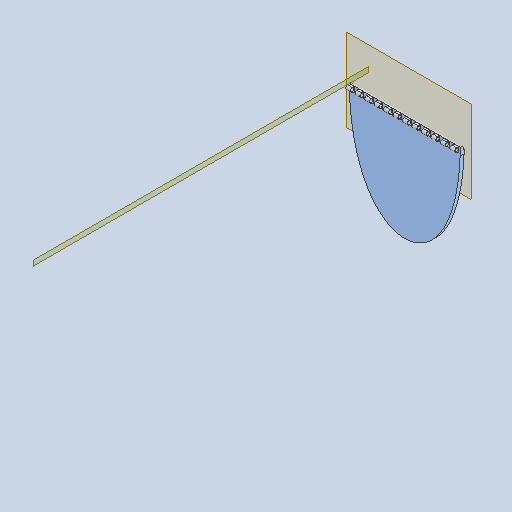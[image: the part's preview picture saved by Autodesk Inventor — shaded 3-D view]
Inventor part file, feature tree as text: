
AUTODESK INVENTOR PART (.ipt)
format: ipt  version: 2023 (Build 270158030, 158C)  size: 225,792 bytes
history: native  units: mm
features: other x4, plane x2, extrude x2, sketch x2, fillet x1, pattern_linear x1, reference x1
ambient origin geometry x8: Origin, YZ Plane, XZ Plane, XY Plane, X Axis, Y Axis, Z Axis, Center Point
bodies: Body1 (feature_tree)
feature tree (13):
  other  "back-flap"
  plane  "Work Plane1"
  extrude  "Extrusion1"  Depth=850.0mm
  plane  "Work Plane2"
  extrude  "Extrusion2"  Depth=30.0mm
  fillet  "Fillet1"  Radius=30.0mm
  pattern_linear  "Rectangular Pattern1"  Count1=35  [1 undecoded]
  sketch  "Sketch1"  dims[d0=50.0mm d1=850.0mm]
  reference  "Reference1"
  sketch  "Sketch3"  dims[d2=700.0mm d3=30.0mm d4=30.0mm d5=350.0mm d6=350.0mm d7=25.0mm d8=0.0mm d11=12.5mm d12=2.5mm d13=20.0mm d14=10.0mm d15=3.0mm d16=25.0mm d17=14.0mm d18=12.5mm d19=30.0mm d20=0.0mm d21=25.0mm d22=120.0mm d24=60.0mm]
  other  "<userpath>\Documents\0004-inventor\3D-CAD-main\primary-engineer-bench.iam"
  other  "primary-engineer-bench.iam"
  other  "bed-base:1"
note: 1 required parameter value undecoded (feature->parameter linkage not recoverable at this tier; creation-order binding heuristic only, values carry confidence <= 0.55)
